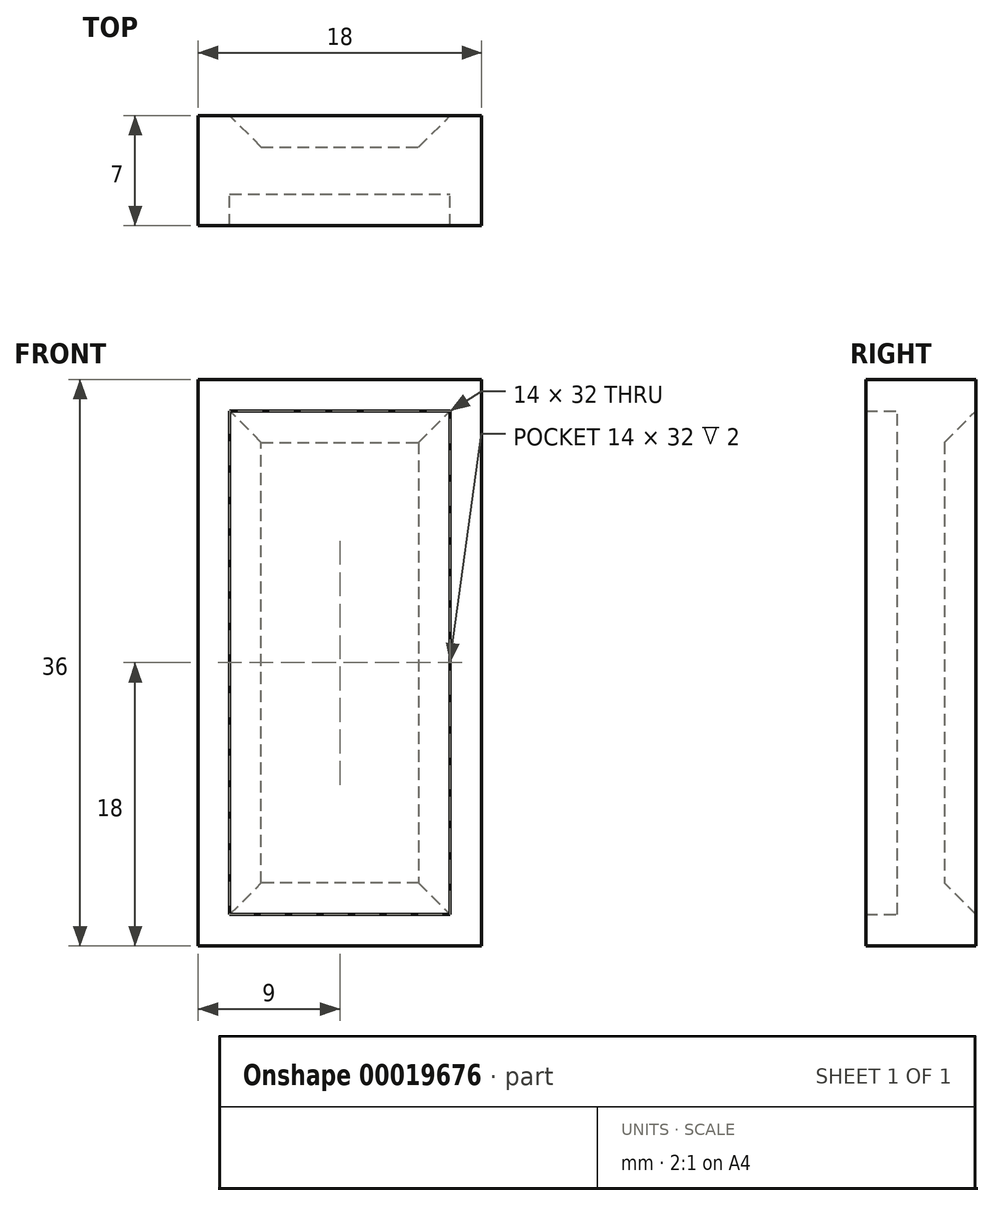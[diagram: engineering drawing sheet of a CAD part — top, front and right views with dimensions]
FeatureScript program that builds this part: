
annotation { "Feature Type Name" : "Feature", "Feature Type Description" : "" }
export const myFeature = defineFeature(function(context is Context, id is Id, definition is map)
    precondition{}
    {
        {
            var Q0;
            Q0=qCreatedBy(makeId("Front.planeOp"),FACE);
            var sketch = newSketch(context, id + "F0", { "sketchPlane" : qUnion([Q0])});
            skLineSegment(sketch, "E0.bottom", {"start": v(0, 0) * mm, "end": v(14, 0) * mm});
            skLineSegment(sketch, "E0.top", {"start": v(0, 32) * mm, "end": v(14, 32) * mm});
            skLineSegment(sketch, "E0.left", {"start": v(0, 0) * mm, "end": v(0, 32) * mm});
            skLineSegment(sketch, "E0.right", {"start": v(14, 0) * mm, "end": v(14, 32) * mm});
            skLineSegment(sketch, "E1.bottom", {"start": v(-2, 34) * mm, "end": v(16, 34) * mm});
            skLineSegment(sketch, "E1.top", {"start": v(-2, -2) * mm, "end": v(16, -2) * mm});
            skLineSegment(sketch, "E1.left", {"start": v(-2, 34) * mm, "end": v(-2, -2) * mm});
            skLineSegment(sketch, "E1.right", {"start": v(16, 34) * mm, "end": v(16, -2) * mm});
            skSolve(sketch);
        }
        {
            var Q0;
            Q0=makeQuery(id+"F0.imprint","IMPRINT",FACE,{"disambiguationData":[TD([[makeQuery(id+"F0.imprint","IMPRINT",EDGE,{"derivedFrom":sQuery(id+"F0.wireOp",EDGE,"E0.bottom")}),-1.0]])]});
            extrude(context, id + "F1", {"entities" : qUnion([Q0]), "endBound" : BoundingType.SYMMETRIC, "depth" : 7 * mm});
        }
        {
            var Q0;
            Q0=makeQuery(id+"F0.imprint","IMPRINT",FACE,{"disambiguationData":[TD([[makeQuery(id+"F0.imprint","IMPRINT",EDGE,{"derivedFrom":sQuery(id+"F0.wireOp",EDGE,"E0.bottom")}),1.0]])]});
            extrude(context, id + "F2", {"entities" : qUnion([Q0]), "operationType" : NewBodyOperationType.ADD, "endBound" : BoundingType.SYMMETRIC, "depth" : 3 * mm});
        }
        {
            var Q0;
            Q0=makeQuery(id+"F2.opExtrude","CAP_EDGE",EDGE,{"disambiguationData":[OSD([sQuery(id+"F0.wireOp",EDGE,"E0.left")])],"isStart":false});
            var Q1;
            Q1=makeQuery(id+"F2.opExtrude","CAP_EDGE",EDGE,{"disambiguationData":[OSD([sQuery(id+"F0.wireOp",EDGE,"E0.bottom")])],"isStart":false});
            var Q2;
            Q2=makeQuery(id+"F2.opExtrude","CAP_EDGE",EDGE,{"disambiguationData":[OSD([sQuery(id+"F0.wireOp",EDGE,"E0.top")])],"isStart":false});
            var Q3;
            Q3=makeQuery(id+"F2.opExtrude","CAP_EDGE",EDGE,{"disambiguationData":[OSD([sQuery(id+"F0.wireOp",EDGE,"E0.right")])],"isStart":false});
            var Q4;
            Q4=makeQuery(id+"F2.opExtrude","CAP_EDGE",EDGE,{"disambiguationData":[OSD([sQuery(id+"F0.wireOp",EDGE,"E0.right")])],"isStart":true});
            var Q5;
            Q5=makeQuery(id+"F2.opExtrude","CAP_EDGE",EDGE,{"disambiguationData":[OSD([sQuery(id+"F0.wireOp",EDGE,"E0.left")])],"isStart":true});
            var Q6;
            Q6=makeQuery(id+"F2.opExtrude","CAP_EDGE",EDGE,{"disambiguationData":[OSD([sQuery(id+"F0.wireOp",EDGE,"E0.bottom")])],"isStart":true});
            var Q7;
            Q7=makeQuery(id+"F2.opExtrude","CAP_EDGE",EDGE,{"disambiguationData":[OSD([sQuery(id+"F0.wireOp",EDGE,"E0.top")])],"isStart":true});
            chamfer(context, id + "F3", {"entities" : qUnion([Q0, Q1, Q2, Q3, Q4, Q5, Q6, Q7]), "width" : 2 * mm, "tangentPropagation" : true});
        }
    });
